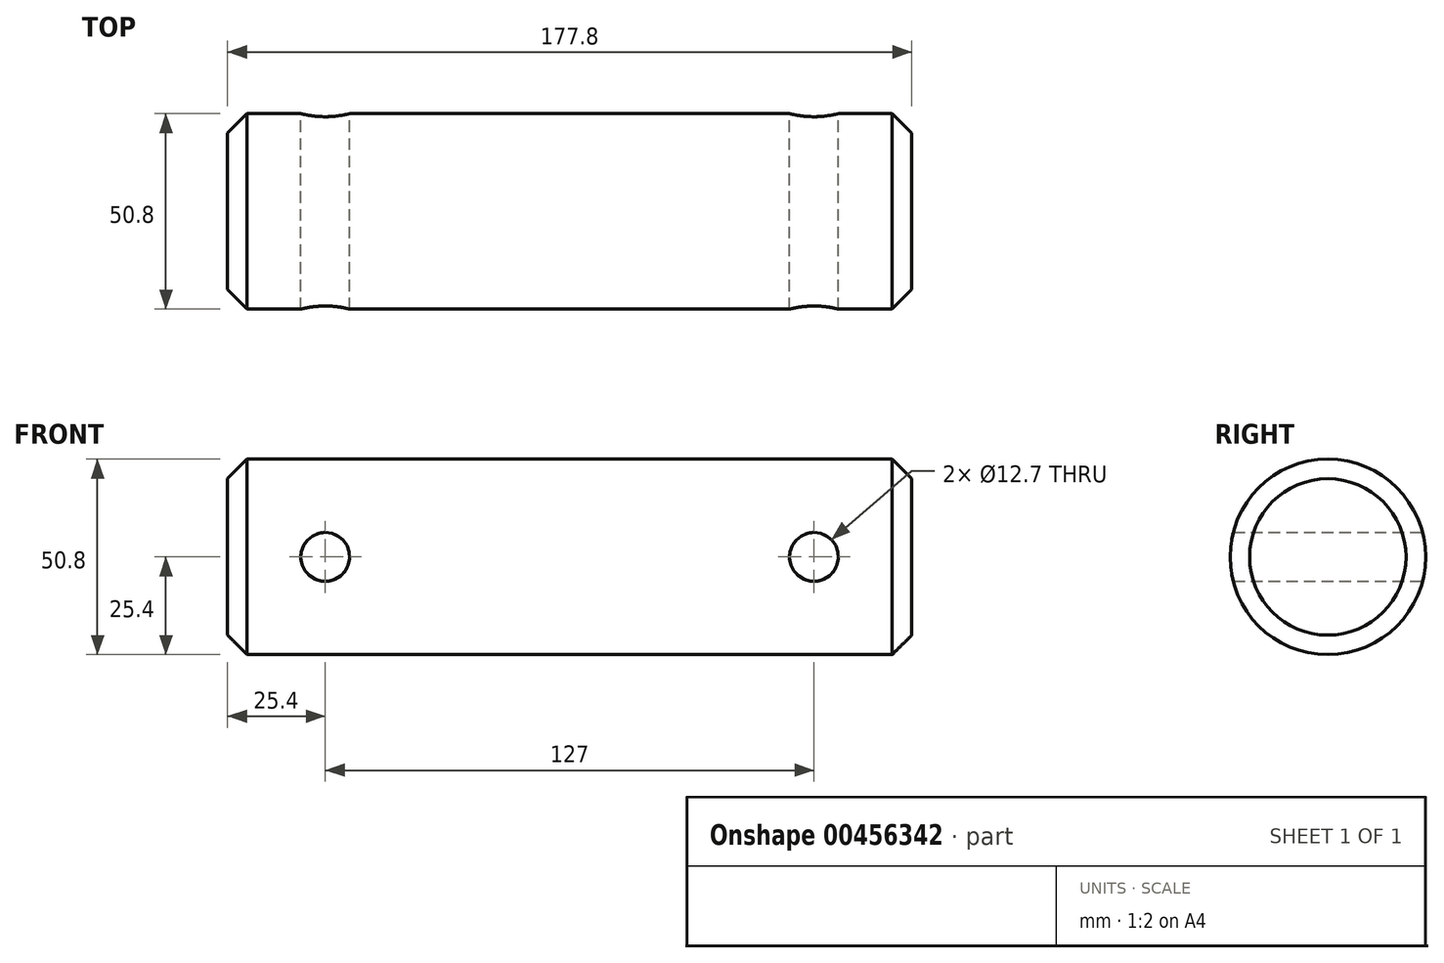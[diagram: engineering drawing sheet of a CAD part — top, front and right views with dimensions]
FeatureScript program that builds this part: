
annotation { "Feature Type Name" : "Feature", "Feature Type Description" : "" }
export const myFeature = defineFeature(function(context is Context, id is Id, definition is map)
    precondition{}
    {
        {
            var Q0;
            Q0=qCreatedBy(makeId("Right.planeOp"),FACE);
            var sketch = newSketch(context, id + "F0", { "sketchPlane" : qUnion([Q0])});
            skCircle(sketch, "E0", {"center": v(0, 0) * mm, "radius": 25.4 * mm});
            skSolve(sketch);
        }
        {
            var Q0;
            Q0=makeQuery(id+"F0.imprint","IMPRINT",FACE,{"disambiguationData":[TD([[makeQuery(id+"F0.imprint","IMPRINT",EDGE,{"derivedFrom":sQuery(id+"F0.wireOp",EDGE,"E0")}),1.0]])]});
            extrude(context, id + "F1", {"entities" : qUnion([Q0]), "depth" : 177.8 * mm});
        }
        {
            var Q0;
            Q0=makeQuery(id+"F1.opExtrude","CAP_EDGE",EDGE,{"disambiguationData":[OSD([sQuery(id+"F0.wireOp",EDGE,"E0")])],"isStart":true});
            var Q1;
            Q1=makeQuery(id+"F1.opExtrude","CAP_EDGE",EDGE,{"disambiguationData":[OSD([sQuery(id+"F0.wireOp",EDGE,"E0")])],"isStart":false});
            chamfer(context, id + "F2", {"entities" : qUnion([Q0, Q1]), "width" : 5.08 * mm, "tangentPropagation" : true});
        }
        {
            var Q0;
            Q0=qCreatedBy(makeId("Front.planeOp"),FACE);
            var sketch = newSketch(context, id + "F3", { "sketchPlane" : qUnion([Q0])});
            skCircle(sketch, "E1", {"center": v(25.4, 0) * mm, "radius": 6.35 * mm});
            skCircle(sketch, "E2", {"center": v(152.4, 0) * mm, "radius": 6.35 * mm});
            skSolve(sketch);
        }
        {
            var Q0;
            Q0=sQuery(id+"F3.wireOp",VERTEX,"E2.center");
            var Q1;
            Q1=sQuery(id+"F3.wireOp",VERTEX,"E1.center");
            var Q2;
            Q2=makeQuery(id+"F1.opExtrude","SWEPT_BODY",BODY,{"disambiguationData":[OSD([sQuery(id+"F0.wireOp",EDGE,"E0")])]});
            hole(context, id + "F4", {"style" : HoleStyle.SIMPLE, "endStyle" : HoleEndStyle.THROUGH, "oppositeDirection" : true, "holeDiameter" : 12.7 * mm, "isTappedThrough" : true, "tappedDepth" : 12.7 * mm, "tapClearance" : 3, "locations" : qUnion([Q0, Q1]), "scope" : qUnion([Q2])});
        }
        {
            var Q0;
            Q0=sQuery(id+"F3.wireOp",VERTEX,"E1.center");
            var Q1;
            Q1=sQuery(id+"F3.wireOp",VERTEX,"E2.center");
            var Q2;
            Q2=makeQuery(id+"F1.opExtrude","SWEPT_BODY",BODY,{"disambiguationData":[OSD([sQuery(id+"F0.wireOp",EDGE,"E0")])]});
            hole(context, id + "F5", {"style" : HoleStyle.SIMPLE, "endStyle" : HoleEndStyle.THROUGH, "holeDiameter" : 12.7 * mm, "isTappedThrough" : true, "tappedDepth" : 12.7 * mm, "tapClearance" : 3, "locations" : qUnion([Q0, Q1]), "scope" : qUnion([Q2])});
        }
    });
